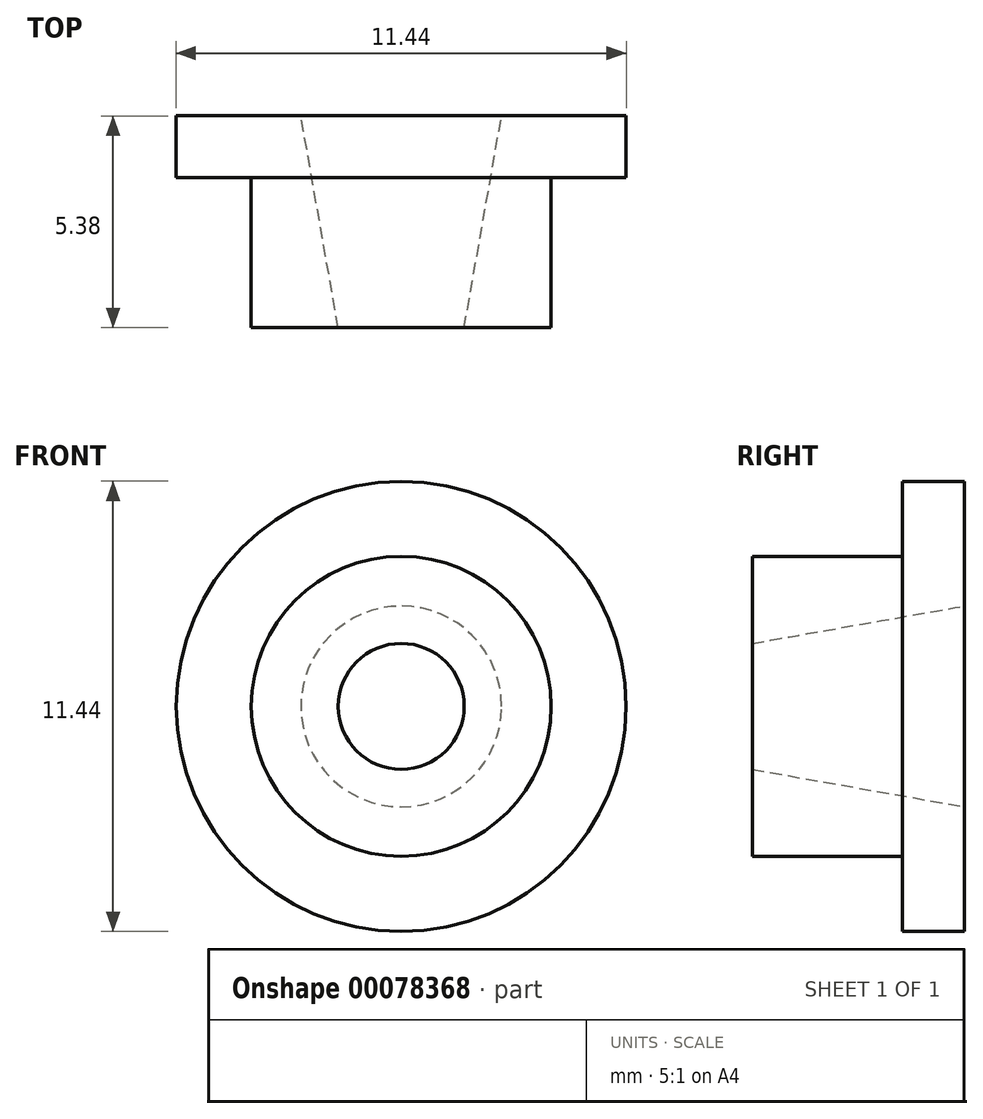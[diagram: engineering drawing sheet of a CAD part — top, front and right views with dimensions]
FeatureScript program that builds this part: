
annotation { "Feature Type Name" : "Feature", "Feature Type Description" : "" }
export const myFeature = defineFeature(function(context is Context, id is Id, definition is map)
    precondition{}
    {
        {
            var Q0;
            Q0=qCreatedBy(makeId("Front.planeOp"),FACE);
            var sketch = newSketch(context, id + "F0", { "sketchPlane" : qUnion([Q0])});
            skCircle(sketch, "E0", {"center": v(0, 0) * mm, "radius": 3.81 * mm});
            skSolve(sketch);
        }
        {
            var Q0;
            Q0 = qSketchRegion(id + "F0", true);
            extrude(context, id + "F1", {"entities" : qUnion([Q0]), "depth" : 3.8 * mm});
        }
        {
            var Q0;
            Q0=makeQuery(id+"F1.opExtrude","CAP_FACE",FACE,{"disambiguationData":[OSD([sQuery(id+"F0.wireOp",EDGE,"E0")])],"isStart":true});
            var sketch = newSketch(context, id + "F2", { "sketchPlane" : qUnion([Q0])});
            skCircle(sketch, "E1", {"center": v(0, 0) * mm, "radius": 5.72 * mm});
            skSolve(sketch);
        }
        {
            var Q0;
            Q0 = qSketchRegion(id + "F2", true);
            extrude(context, id + "F3", {"entities" : qUnion([Q0]), "operationType" : NewBodyOperationType.ADD, "depth" : 1.57 * mm});
        }
        {
            var Q0;
            Q0=qCreatedBy(makeId("Right.planeOp"),FACE);
            var sketch = newSketch(context, id + "F4", { "sketchPlane" : qUnion([Q0])});
            skLineSegment(sketch, "E2", {"start": v(-3.88, 0) * mm, "end": v(1.65, 0) * mm});
            skLineSegment(sketch, "E3", {"start": v(-3.88, 0) * mm, "end": v(-3.88, 1.59) * mm});
            skLineSegment(sketch, "E4", {"start": v(-3.88, 1.59) * mm, "end": v(1.65, 2.56) * mm});
            skLineSegment(sketch, "E5", {"start": v(1.65, 0) * mm, "end": v(1.65, 2.56) * mm});
            skSolve(sketch);
        }
        {
            var Q0;
            Q0 = qSketchRegion(id + "F4", true);
            var Q1;
            Q1=sQuery(id+"F4.wireOp",EDGE,"E2");
            revolve(context, id + "F5", {"operationType" : NewBodyOperationType.REMOVE, "entities" : qUnion([Q0]), "axis" : qUnion([Q1]), "revolveType" : RevolveType.FULL, "oppositeDirection" : true});
        }
    });
